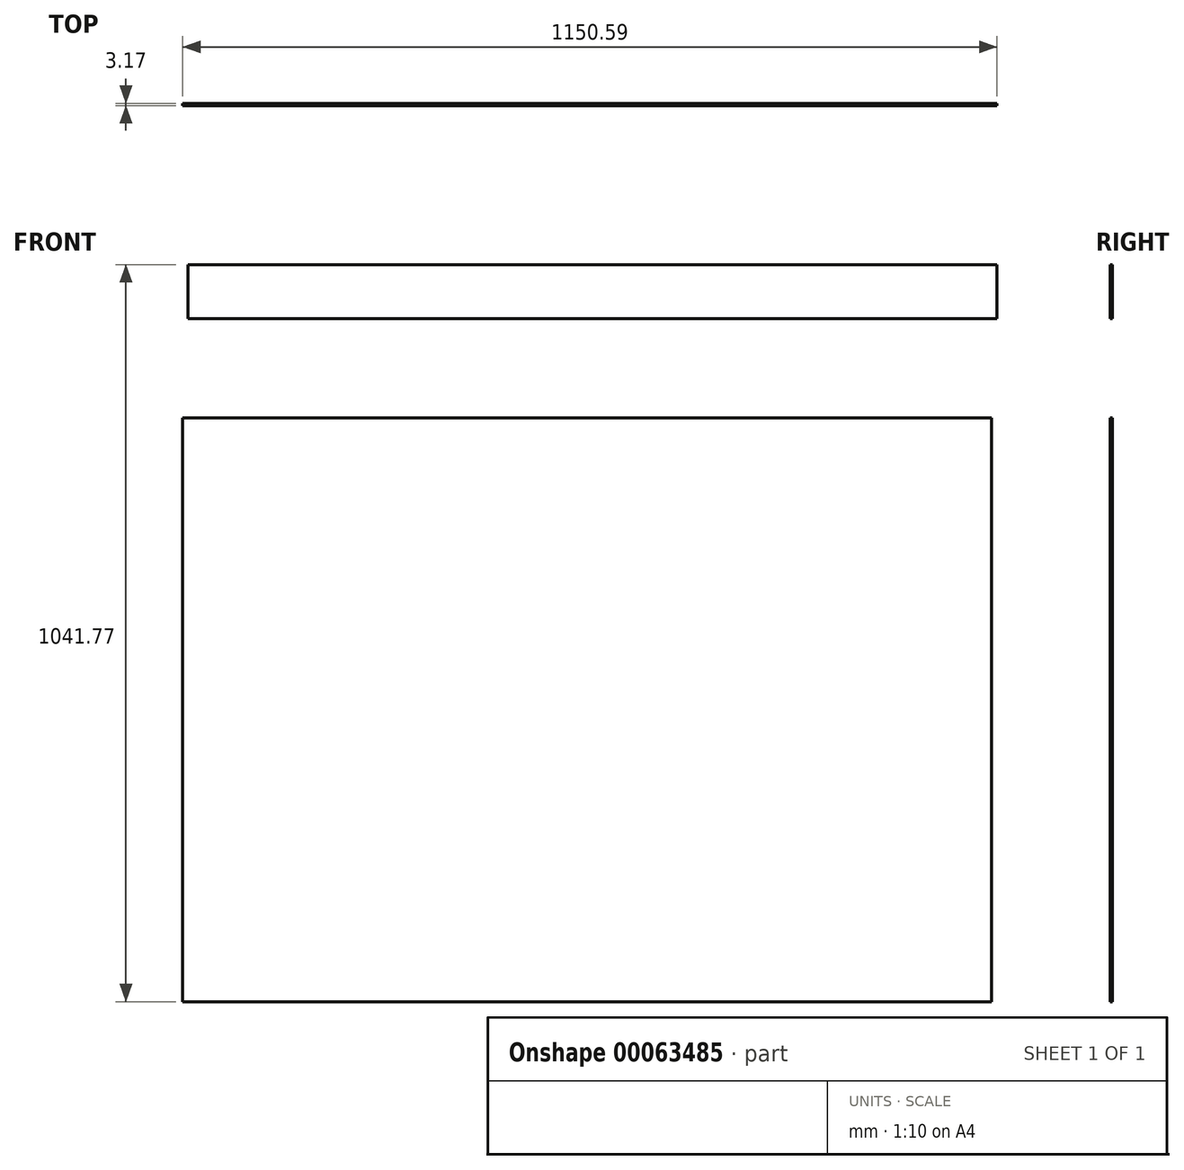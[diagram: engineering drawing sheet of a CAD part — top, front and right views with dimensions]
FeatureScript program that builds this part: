
annotation { "Feature Type Name" : "Feature", "Feature Type Description" : "" }
export const myFeature = defineFeature(function(context is Context, id is Id, definition is map)
    precondition{}
    {
        {
            var Q0;
            Q0=qCreatedBy(makeId("Front.planeOp"),FACE);
            var sketch = newSketch(context, id + "F0", { "sketchPlane" : qUnion([Q0])});
            skLineSegment(sketch, "E0.bottom", {"start": v(-577.77, 446.76) * mm, "end": v(565.23, 446.76) * mm});
            skLineSegment(sketch, "E0.top", {"start": v(-577.77, -378.74) * mm, "end": v(565.23, -378.74) * mm});
            skLineSegment(sketch, "E0.left", {"start": v(-577.77, 446.76) * mm, "end": v(-577.77, -378.74) * mm});
            skLineSegment(sketch, "E0.right", {"start": v(565.23, 446.76) * mm, "end": v(565.23, -378.74) * mm});
            skLineSegment(sketch, "E1.bottom", {"start": v(572.82, 663.03) * mm, "end": v(-570.18, 663.03) * mm});
            skLineSegment(sketch, "E1.top", {"start": v(572.82, 586.83) * mm, "end": v(-570.18, 586.83) * mm});
            skLineSegment(sketch, "E1.left", {"start": v(572.82, 663.03) * mm, "end": v(572.82, 586.83) * mm});
            skLineSegment(sketch, "E1.right", {"start": v(-570.18, 663.03) * mm, "end": v(-570.18, 586.83) * mm});
            skSolve(sketch);
        }
        {
            var Q0;
            Q0=makeQuery(id+"F0.imprint","IMPRINT",FACE,{"disambiguationData":[TD([[makeQuery(id+"F0.imprint","IMPRINT",EDGE,{"derivedFrom":sQuery(id+"F0.wireOp",EDGE,"E0.bottom")}),-1.0]])]});
            var Q1;
            Q1=makeQuery(id+"F0.imprint","IMPRINT",FACE,{"disambiguationData":[TD([[makeQuery(id+"F0.imprint","IMPRINT",EDGE,{"derivedFrom":sQuery(id+"F0.wireOp",EDGE,"E1.bottom")}),1.0]])]});
            extrude(context, id + "F1", {"entities" : qUnion([Q0, Q1]), "depth" : 3.17 * mm});
        }
    });
